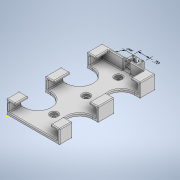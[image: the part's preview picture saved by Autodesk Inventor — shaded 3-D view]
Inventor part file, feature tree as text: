
AUTODESK INVENTOR PART (.ipt)
format: ipt  version: 2020.2 (Build 242310000, 310)  size: 691,712 bytes
history: native  units: in
note: dims shown in document units (in); Inventor stores cm internally (conversion verified against a paired STEP export)
features: sketch x10, extrude x7, fillet x6, other x3, hole x2
ambient origin geometry x8: Origin, YZ Plane, XZ Plane, XY Plane, X Axis, Y Axis, Z Axis, Center Point
bodies: Solid1 (feature_tree)
feature tree (28):
  other  "Annotations"
  extrude  "Extrusion1"  Depth=0.8in
  extrude  "Extrusion2"  Depth=0.5in
  extrude  "Extrusion3"  Depth=0.5in
  extrude  "Extrusion4"  Depth=0.8in
  hole  "Hole1"  [1 undecoded]
  sketch  "Sketch9"  dims[d12=0.15in d13=0.15in]
  extrude  "Extrusion5"  Depth=0.15in
  extrude  "Extrusion6"  Depth=0.3in
  fillet  "Fillet1"  Radius=0.3in
  fillet  "Fillet2"  Radius=0.3in
  fillet  "Fillet3"  Radius=0.3in
  fillet  "Fillet4"  Radius=0.15in
  fillet  "Fillet5"  Radius=0.15in
  extrude  "Extrusion7"  Depth=0.2in
  sketch  "Sketch12"  dims[d24=0.15in d25=0.15in d26=0.15in]
  hole  "Hole2"  [1 undecoded]
  fillet  "Fillet6"  Radius=0.15in
  sketch  "Sketch1"  dims[d0=3.3in d1=0.8in]
  sketch  "Sketch2"  dims[d2=5.8in d5=0.5in]
  sketch  "Sketch3"  dims[d6=1.0in d7=0.5in]
  sketch  "Sketch5"  dims[d8=1.0in d9=0.8in]
  sketch  "Sketch6"  dims[d10=0.2in d11=0.4in]
  sketch  "Sketch10"  dims[d14=0.77in d15=0.3in d16=0.3in d17=0.3in d18=0.3in d19=0.15in d20=0.15in]
  sketch  "Sketch11"  dims[d21=0.2in d22=0.0in d23=0.15in]
  sketch  "Sketch13"  dims[d27=0.15in d28=0.15in d29=0.15in d30=0.15in d31=0.15in d32=0.09in d33=0.15in d34=0.09in d35=0.68in d36=0.0in d37=0.15in d38=0.0in d39=0.09in d40=0.15in d41=0.09in d42=0.15in d43=0.25in d44=0.0in d45=0.12in d46=0.75in d47=0.375in d48=0.25in d49=0.5635in d50=0.4in d51=0.8108in d55=0.15in d56=0.15in d57=0.15in d58=0.15in d59=0.8in d60=0.15in d61=0.4in d62=0.0in d63=0.4in d64=0.0in d65=0.8in d66=0.05in d67=0.05in d68=0.125in d69=0.05in d76=0.5in d77=1.0in d78=0.1in d79=0.2in d80=0.1in d81=0.0in d82=1.5in d83=1.5in d84=0.5in d85=0.1in d86=0.5in d87=0.1in d88=1.0in d89=0.2in d90=1.0in d91=0.2in d92=0.75in d93=0.4in d94=0.15in d95=0.5635in d96=0.4in d97=0.8108in d98=0.05in d70=0.1543in d71=0.3044in d72=0.7in d73=0.2993in d74=0.3805in d75=0.6613in]
  other  "Linear Dimension 1"
  other  "Linear Dimension 2"
note: 2 required parameter values undecoded (feature->parameter linkage not recoverable at this tier; creation-order binding heuristic only, values carry confidence <= 0.55)
